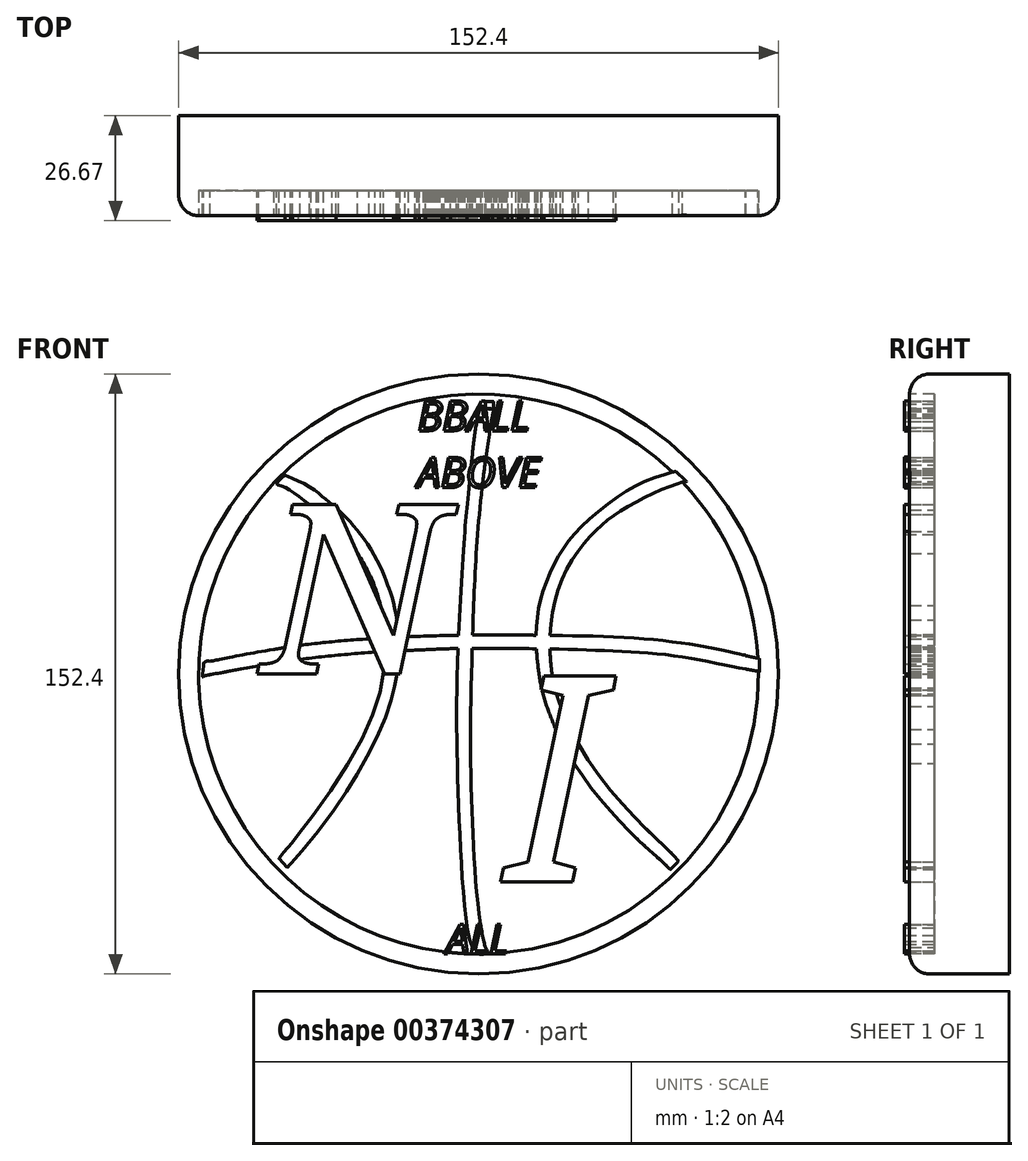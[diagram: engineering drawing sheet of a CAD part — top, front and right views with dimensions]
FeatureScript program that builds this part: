
annotation { "Feature Type Name" : "Feature", "Feature Type Description" : "" }
export const myFeature = defineFeature(function(context is Context, id is Id, definition is map)
    precondition{}
    {
        {
            var Q0;
            Q0=qCreatedBy(makeId("Front.planeOp"),FACE);
            var sketch = newSketch(context, id + "F0", { "sketchPlane" : qUnion([Q0])});
            skCircle(sketch, "E0", {"center": v(0, 0) * mm, "radius": 76.2 * mm});
            skSolve(sketch);
        }
        {
            var Q0;
            Q0 = qSketchRegion(id + "F0", true);
            extrude(context, id + "F1", {"entities" : qUnion([Q0]), "depth" : 25.4 * mm});
        }
        {
            var Q0;
            Q0=makeQuery(id+"F1.opExtrude","CAP_EDGE",EDGE,{"disambiguationData":[OSD([sQuery(id+"F0.wireOp",EDGE,"E0")])],"isStart":false});
            fillet(context, id + "F2", {"entities" : qUnion([Q0]), "radius" : 5.08 * mm, "tangentPropagation" : true, "allowEdgeOverflow" : false});
        }
        {
            var Q0;
            Q0=makeQuery(id+"F1.opExtrude","CAP_FACE",FACE,{"disambiguationData":[OSD([sQuery(id+"F0.wireOp",EDGE,"E0")])],"isStart":false});
            extrude(context, id + "F3", {"entities" : qUnion([Q0]), "operationType" : NewBodyOperationType.REMOVE, "oppositeDirection" : true, "depth" : 6.35 * mm});
        }
        {
            var Q0;
            Q0=qCreatedBy(makeId("Front.planeOp"),FACE);
            var sketch = newSketch(context, id + "F4", { "sketchPlane" : qUnion([Q0])});
            skFitSpline(sketch, "E1", {"points": [v(0.43, 67.37) * mm, v(-2.38, 48.32) * mm, v(-3.55, 35.89) * mm, v(-5.39, 2.5) * mm, v(-5.39, -23.76) * mm, v(-3.75, -57.29) * mm, v(0, -71.12) * mm, v(2.35, -70.65) * mm, v(2.07, -70.11) * mm, v(0, -60.03) * mm, v(-1.58, -38.52) * mm, v(-2.06, -14.54) * mm, v(-1.46, 12.15) * mm, v(0.45, 43.52) * mm, v(3.56, 65.82) * mm, v(3.73, 67.22) * mm, v(3.43, 67.3) * mm, v(2.66, 67.36) * mm, v(1.7, 67.42) * mm, v(0.96, 67.42) * mm, v(0.43, 67.37) * mm]});
            skFitSpline(sketch, "E2", {"points": [v(0.43, 67.37) * mm, v(0.96, 69.23) * mm, v(1.24, 69.3) * mm, v(3.73, 69.24) * mm, v(3.73, 69.12) * mm, v(3.73, 67.22) * mm, v(3.43, 67.3) * mm, v(0.96, 67.42) * mm, v(0.43, 67.37) * mm]});
            skFitSpline(sketch, "E3", {"points": [v(-51.3, 48.31) * mm, v(-49.2, 50.52) * mm, v(-49.04, 50.46) * mm, v(-43.77, 48.04) * mm, v(-39.04, 44.55) * mm, v(-36.11, 42.16) * mm, v(-32.27, 38.2) * mm, v(-28.61, 33.53) * mm, v(-24.96, 27.16) * mm, v(-23.18, 22.83) * mm, v(-22.06, 19.63) * mm, v(-20.74, 13.35) * mm, v(-20.42, 9.42) * mm, v(-20.3, 5.87) * mm, v(-20.63, 0.66) * mm, v(-21.52, -3.9) * mm, v(-23.9, -11.73) * mm, v(-29.79, -23.62) * mm, v(-36.43, -34.1) * mm, v(-46.85, -47.27) * mm, v(-48.45, -49.12) * mm, v(-48.49, -49.2) * mm, v(-50.8, -46.83) * mm, v(-50.84, -46.8) * mm, v(-48.26, -43.86) * mm, v(-46.16, -41.3) * mm, v(-34.02, -24.2) * mm, v(-25.35, -5.66) * mm, v(-23.77, 5.77) * mm, v(-24.56, 15.63) * mm, v(-28.4, 26.67) * mm, v(-36.59, 37.72) * mm, v(-44.97, 44.62) * mm, v(-50.1, 47.77) * mm, v(-51.3, 48.31) * mm]});
            skFitSpline(sketch, "E4", {"points": [v(49.97, 51.4) * mm, v(43.74, 49.51) * mm, v(35.15, 44.88) * mm, v(25.97, 37.27) * mm, v(21.1, 31.24) * mm, v(17.5, 24.26) * mm, v(15.31, 16.84) * mm, v(14.6, 9.88) * mm, v(15.03, 2.38) * mm, v(16.3, -4.84) * mm, v(18.7, -11.92) * mm, v(21.92, -18.8) * mm, v(28.03, -28.15) * mm, v(35.89, -37.45) * mm, v(43, -44.46) * mm, v(48.51, -49.6) * mm, v(48.64, -49.74) * mm, v(50.75, -47.69) * mm, v(50.82, -47.62) * mm, v(48.93, -45.5) * mm, v(41.94, -38.73) * mm, v(30.38, -25.58) * mm, v(21.37, -9.65) * mm, v(18.22, 4.2) * mm, v(20.6, 22.67) * mm, v(28.83, 35.42) * mm, v(35.86, 41.28) * mm, v(46.79, 46.95) * mm, v(52.6, 48.86) * mm, v(52.81, 48.9) * mm, v(50.42, 51.15) * mm, v(49.97, 51.4) * mm]});
            skFitSpline(sketch, "E5", {"points": [v(-68.51, 3.2) * mm, v(-68.41, 0) * mm, v(-68.4, 0) * mm, v(-56.64, 2.03) * mm, v(-36.74, 4.8) * mm, v(-23.77, 5.77) * mm, v(-20.3, 5.87) * mm, v(-5.24, 6.48) * mm, v(14.69, 6.44) * mm, v(33.73, 5.87) * mm, v(51.34, 4.39) * mm, v(66.6, 1.45) * mm, v(71.32, 0.61) * mm, v(71.34, 0.61) * mm, v(71.35, 3.86) * mm, v(71.26, 3.94) * mm, v(64.45, 5.36) * mm, v(53.3, 7.57) * mm, v(40.26, 8.93) * mm, v(28.65, 9.56) * mm, v(18.16, 9.8) * mm, v(5.3, 9.9) * mm, v(-1.53, 9.86) * mm, v(-7.08, 9.78) * mm, v(-18.44, 9.42) * mm, v(-20.42, 9.42) * mm, v(-27.54, 8.86) * mm, v(-35.46, 8.26) * mm, v(-48.96, 6.71) * mm, v(-64.6, 3.96) * mm, v(-68.02, 3.27) * mm, v(-68.48, 3.2) * mm, v(-68.51, 3.2) * mm, v(-68.51, 3.2) * mm]});
            skSolve(sketch);
        }
        {
            var Q0;
            {var subQ0=sQuery(id+"F4.wireOp",EDGE,"E5");var subQ1=sQuery(id+"F4.wireOp",EDGE,"E1");var subQ2=makeQuery(id+"F4.imprint","INTERSECT",VERTEX,{"disambiguationData":[OD(1.0)],"derivedFrom":[subQ1,subQ0]});Q0=makeQuery(id+"F4.imprint","IMPRINT",FACE,{"disambiguationData":[TD([[makeQuery(id+"F4.imprint","IMPRINT",EDGE,{"disambiguationData":[TD([[subQ2,-1.0]])],"derivedFrom":subQ1}),1.0]])]});}
            var Q1;
            {var subQ0=sQuery(id+"F4.wireOp",EDGE,"E5");var subQ1=sQuery(id+"F4.wireOp",EDGE,"E3");var subQ2=makeQuery(id+"F4.imprint","INTERSECT",VERTEX,{"disambiguationData":[OD(0.0)],"derivedFrom":[subQ1,subQ0]});Q1=makeQuery(id+"F4.imprint","IMPRINT",FACE,{"disambiguationData":[TD([[makeQuery(id+"F4.imprint","IMPRINT",EDGE,{"disambiguationData":[TD([[subQ2,-1.0]])],"derivedFrom":subQ1}),-1.0]])]});}
            var Q2;
            {var subQ0=sQuery(id+"F4.wireOp",EDGE,"E5");var subQ1=sQuery(id+"F4.wireOp",EDGE,"E3");var subQ2=makeQuery(id+"F4.imprint","INTERSECT",VERTEX,{"disambiguationData":[OD(2.0)],"derivedFrom":[subQ1,subQ0]});Q2=makeQuery(id+"F4.imprint","IMPRINT",FACE,{"disambiguationData":[TD([[makeQuery(id+"F4.imprint","IMPRINT",EDGE,{"disambiguationData":[TD([[subQ2,-1.0]])],"derivedFrom":subQ1}),1.0]])]});}
            var Q3;
            {var subQ0=sQuery(id+"F4.wireOp",EDGE,"E5");var subQ1=sQuery(id+"F4.wireOp",EDGE,"E3");var subQ2=makeQuery(id+"F4.imprint","INTERSECT",VERTEX,{"disambiguationData":[OD(1.0)],"derivedFrom":[subQ1,subQ0]});Q3=makeQuery(id+"F4.imprint","IMPRINT",FACE,{"disambiguationData":[TD([[makeQuery(id+"F4.imprint","IMPRINT",EDGE,{"disambiguationData":[TD([[subQ2,1.0]])],"derivedFrom":subQ1}),-1.0]])]});}
            var Q4;
            {var subQ0=sQuery(id+"F4.wireOp",EDGE,"E5");var subQ1=sQuery(id+"F4.wireOp",EDGE,"E4");var subQ2=makeQuery(id+"F4.imprint","INTERSECT",VERTEX,{"disambiguationData":[OD(0.0)],"derivedFrom":[subQ1,subQ0]});Q4=makeQuery(id+"F4.imprint","IMPRINT",FACE,{"disambiguationData":[TD([[makeQuery(id+"F4.imprint","IMPRINT",EDGE,{"disambiguationData":[TD([[subQ2,-1.0]])],"derivedFrom":subQ1}),1.0]])]});}
            var Q5;
            {var subQ0=sQuery(id+"F4.wireOp",EDGE,"E5");var subQ1=sQuery(id+"F4.wireOp",EDGE,"E4");var subQ2=makeQuery(id+"F4.imprint","INTERSECT",VERTEX,{"disambiguationData":[OD(2.0)],"derivedFrom":[subQ1,subQ0]});Q5=makeQuery(id+"F4.imprint","IMPRINT",FACE,{"disambiguationData":[TD([[makeQuery(id+"F4.imprint","IMPRINT",EDGE,{"disambiguationData":[TD([[subQ2,-1.0]])],"derivedFrom":subQ1}),-1.0]])]});}
            var Q6;
            {var subQ0=sQuery(id+"F4.wireOp",EDGE,"E5");var subQ1=sQuery(id+"F4.wireOp",EDGE,"E4");var subQ2=makeQuery(id+"F4.imprint","INTERSECT",VERTEX,{"disambiguationData":[OD(1.0)],"derivedFrom":[subQ1,subQ0]});Q6=makeQuery(id+"F4.imprint","IMPRINT",FACE,{"disambiguationData":[TD([[makeQuery(id+"F4.imprint","IMPRINT",EDGE,{"disambiguationData":[TD([[subQ2,1.0]])],"derivedFrom":subQ1}),1.0]])]});}
            var Q7;
            {var subQ0=sQuery(id+"F4.wireOp",EDGE,"E5");var subQ1=sQuery(id+"F4.wireOp",EDGE,"E1");var subQ2=makeQuery(id+"F4.imprint","INTERSECT",VERTEX,{"disambiguationData":[OD(0.0)],"derivedFrom":[subQ1,subQ0]});Q7=makeQuery(id+"F4.imprint","IMPRINT",FACE,{"disambiguationData":[TD([[makeQuery(id+"F4.imprint","IMPRINT",EDGE,{"disambiguationData":[TD([[subQ2,-1.0]])],"derivedFrom":subQ1}),-1.0]])]});}
            var Q8;
            {var subQ0=sQuery(id+"F4.wireOp",EDGE,"E5");var subQ1=sQuery(id+"F4.wireOp",EDGE,"E1");var subQ2=makeQuery(id+"F4.imprint","INTERSECT",VERTEX,{"disambiguationData":[OD(2.0)],"derivedFrom":[subQ1,subQ0]});Q8=makeQuery(id+"F4.imprint","IMPRINT",FACE,{"disambiguationData":[TD([[makeQuery(id+"F4.imprint","IMPRINT",EDGE,{"disambiguationData":[TD([[subQ2,-1.0]])],"derivedFrom":subQ1}),-1.0]])]});}
            var Q9;
            {var subQ0=sQuery(id+"F4.wireOp",EDGE,"E2");var subQ1=sQuery(id+"F4.wireOp",EDGE,"E1");var subQ2=makeQuery(id+"F4.imprint","INTERSECT",VERTEX,{"disambiguationData":[OD(1.0)],"derivedFrom":[subQ1,subQ0]});Q9=makeQuery(id+"F4.imprint","IMPRINT",FACE,{"disambiguationData":[TD([[makeQuery(id+"F4.imprint","IMPRINT",EDGE,{"disambiguationData":[TD([[subQ2,-1.0]])],"derivedFrom":subQ1}),1.0]])]});}
            var Q10;
            {var subQ0=sQuery(id+"F4.wireOp",EDGE,"E2");var subQ1=sQuery(id+"F4.wireOp",EDGE,"E1");var subQ2=makeQuery(id+"F4.imprint","INTERSECT",VERTEX,{"disambiguationData":[OD(0.0)],"derivedFrom":[subQ1,subQ0]});Q10=makeQuery(id+"F4.imprint","IMPRINT",FACE,{"disambiguationData":[TD([[makeQuery(id+"F4.imprint","IMPRINT",EDGE,{"disambiguationData":[TD([[subQ2,1.0]])],"derivedFrom":subQ1}),1.0]])]});}
            var Q11;
            {var subQ0=sQuery(id+"F4.wireOp",EDGE,"E2");var subQ1=sQuery(id+"F4.wireOp",EDGE,"E1");var subQ2=makeQuery(id+"F4.imprint","INTERSECT",VERTEX,{"disambiguationData":[OD(1.0)],"derivedFrom":[subQ1,subQ0]});Q11=makeQuery(id+"F4.imprint","IMPRINT",FACE,{"disambiguationData":[TD([[makeQuery(id+"F4.imprint","IMPRINT",EDGE,{"disambiguationData":[TD([[subQ2,-1.0]])],"derivedFrom":subQ1}),-1.0]])]});}
            var Q12;
            {var subQ1=sQuery(id+"F4.wireOp",EDGE,"E1");var subQ4=sQuery(id+"F4.wireOp",EDGE,"E5");var subQ5=makeQuery(id+"F4.imprint","INTERSECT",VERTEX,{"disambiguationData":[OD(0.0)],"derivedFrom":[subQ1,subQ4]});Q12=makeQuery(id+"F4.imprint","IMPRINT",FACE,{"disambiguationData":[TD([[makeQuery(id+"F4.imprint","IMPRINT",EDGE,{"disambiguationData":[TD([[subQ5,1.0]])],"derivedFrom":subQ1}),1.0]])]});}
            var Q13;
            {var subQ0=sQuery(id+"F4.wireOp",EDGE,"E5");var subQ1=sQuery(id+"F4.wireOp",EDGE,"E1");var subQ2=makeQuery(id+"F4.imprint","INTERSECT",VERTEX,{"disambiguationData":[OD(0.0)],"derivedFrom":[subQ1,subQ0]});Q13=makeQuery(id+"F4.imprint","IMPRINT",FACE,{"disambiguationData":[TD([[makeQuery(id+"F4.imprint","IMPRINT",EDGE,{"disambiguationData":[TD([[subQ2,-1.0]])],"derivedFrom":subQ1}),1.0]])]});}
            var Q14;
            {var subQ0=sQuery(id+"F4.wireOp",EDGE,"E5");var subQ1=sQuery(id+"F4.wireOp",EDGE,"E3");var subQ2=makeQuery(id+"F4.imprint","INTERSECT",VERTEX,{"disambiguationData":[OD(0.0)],"derivedFrom":[subQ1,subQ0]});Q14=makeQuery(id+"F4.imprint","IMPRINT",FACE,{"disambiguationData":[TD([[makeQuery(id+"F4.imprint","IMPRINT",EDGE,{"disambiguationData":[TD([[subQ2,1.0]])],"derivedFrom":subQ1}),-1.0]])]});}
            var Q15;
            {var subQ0=sQuery(id+"F4.wireOp",EDGE,"E5");var subQ1=sQuery(id+"F4.wireOp",EDGE,"E4");var subQ2=makeQuery(id+"F4.imprint","INTERSECT",VERTEX,{"disambiguationData":[OD(0.0)],"derivedFrom":[subQ1,subQ0]});Q15=makeQuery(id+"F4.imprint","IMPRINT",FACE,{"disambiguationData":[TD([[makeQuery(id+"F4.imprint","IMPRINT",EDGE,{"disambiguationData":[TD([[subQ2,1.0]])],"derivedFrom":subQ1}),1.0]])]});}
            extrude(context, id + "F5", {"entities" : qUnion([Q0, Q1, Q2, Q3, Q4, Q5, Q6, Q7, Q8, Q9, Q10, Q11, Q12, Q13, Q14, Q15]), "operationType" : NewBodyOperationType.ADD, "depth" : 25.4 * mm});
        }
        {
            var Q0;
            Q0=qCreatedBy(makeId("Front.planeOp"),FACE);
            var sketch = newSketch(context, id + "F6", { "sketchPlane" : qUnion([Q0])});
            skFitSpline(sketch, "E6", {"points": [v(-69.92, 2.6) * mm, v(-70.1, -0.84) * mm, v(-69.9, -0.68) * mm, v(-67.28, 0) * mm, v(-59.4, 1.42) * mm, v(-45.16, 3.72) * mm, v(-23.73, 5.73) * mm, v(-4.99, 6.47) * mm, v(4.26, 6.5) * mm, v(31.3, 6.07) * mm, v(54, 4.1) * mm, v(67.83, 1.25) * mm, v(67.93, 1.25) * mm, v(67.82, 4.75) * mm, v(67.61, 4.84) * mm, v(59.91, 6.46) * mm, v(38.53, 9.19) * mm, v(12.88, 9.82) * mm, v(-1.6, 9.88) * mm, v(-28.75, 8.88) * mm, v(-55.01, 5.69) * mm, v(-68.06, 3.22) * mm, v(-68.88, 3.3) * mm, v(-69.95, 2.75) * mm, v(-69.92, 2.6) * mm]});
            skSolve(sketch);
        }
        {
            var Q0;
            Q0 = qSketchRegion(id + "F6", true);
            extrude(context, id + "F7", {"entities" : qUnion([Q0]), "depth" : 25.4 * mm});
        }
        {
            var Q0;
            Q0 = qSketchRegion(id + "F4", true);
            extrude(context, id + "F8", {"entities" : qUnion([Q0]), "depth" : 25.4 * mm});
        }
        {
            var Q0;
            Q0 = qSketchRegion(id + "F4", true);
            extrude(context, id + "F9", {"entities" : qUnion([Q0]), "depth" : 25.4 * mm});
        }
        {
            var Q0;
            {var subQ0=sQuery(id+"F4.wireOp",EDGE,"E5");var subQ1=sQuery(id+"F4.wireOp",EDGE,"E1");var subQ2=makeQuery(id+"F4.imprint","INTERSECT",VERTEX,{"disambiguationData":[OD(1.0)],"derivedFrom":[subQ1,subQ0]});var subQ3=sQuery(id+"F4.wireOp",EDGE,"E3");var subQ4=makeQuery(id+"F4.imprint","INTERSECT",VERTEX,{"disambiguationData":[OD(0.0)],"derivedFrom":[subQ3,subQ0]});var subQ5=makeQuery(id+"F4.imprint","INTERSECT",VERTEX,{"disambiguationData":[OD(1.0)],"derivedFrom":[subQ3,subQ0]});var subQ7=makeQuery(id+"F4.imprint","INTERSECT",VERTEX,{"disambiguationData":[OD(2.0)],"derivedFrom":[subQ3,subQ0]});var subQ8=sQuery(id+"F4.wireOp",EDGE,"E2");var subQ9=makeQuery(id+"F4.imprint","INTERSECT",VERTEX,{"disambiguationData":[OD(0.0)],"derivedFrom":[subQ1,subQ8]});var subQ11=sQuery(id+"F0.wireOp",EDGE,"E0");var subQ12=sQuery(id+"F4.wireOp",EDGE,"E4");var subQ13=makeQuery(id+"F4.imprint","INTERSECT",VERTEX,{"disambiguationData":[OD(1.0)],"derivedFrom":[subQ12,subQ0]});var subQ14=makeQuery(id+"F4.imprint","INTERSECT",VERTEX,{"disambiguationData":[OD(0.0)],"derivedFrom":[subQ1,subQ0]});var subQ15=makeQuery(id+"F4.imprint","INTERSECT",VERTEX,{"disambiguationData":[OD(3.0)],"derivedFrom":[subQ1,subQ0]});Q0=makeQuery(id+"F5.boolean.opBoolean","SPLIT",FACE,{"disambiguationData":[TD([makeQuery(id+"F3.boolean.opBoolean","COPY",FACE,{"derivedFrom":makeQuery(id+"F3.opExtrude","SWEPT_FACE",FACE,{"disambiguationData":[OSD([subQ11])]})}),makeQuery(id+"F5.opExtrude","SWEPT_FACE",FACE,{"disambiguationData":[OSD([subQ1]),TDD([makeQuery(id+"F4.imprint","IMPRINT",EDGE,{"disambiguationData":[TD([[subQ14,1.0]])],"derivedFrom":subQ1})])]}),makeQuery(id+"F5.opExtrude","SWEPT_FACE",FACE,{"disambiguationData":[OSD([subQ1]),TDD([makeQuery(id+"F4.imprint","IMPRINT",EDGE,{"disambiguationData":[TD([[subQ2,-1.0]])],"derivedFrom":subQ1})])]}),makeQuery(id+"F5.opExtrude","SWEPT_FACE",FACE,{"disambiguationData":[OSD([subQ1]),TDD([makeQuery(id+"F4.imprint","IMPRINT",EDGE,{"disambiguationData":[TD([[subQ15,-1.0]])],"derivedFrom":subQ1})])]}),makeQuery(id+"F5.opExtrude","SWEPT_FACE",FACE,{"disambiguationData":[OSD([subQ8]),TDD([makeQuery(id+"F4.imprint","IMPRINT",EDGE,{"disambiguationData":[TD([[subQ9,-1.0]])],"derivedFrom":subQ8})])]}),makeQuery(id+"F5.opExtrude","SWEPT_FACE",FACE,{"disambiguationData":[OSD([subQ3]),TDD([makeQuery(id+"F4.imprint","IMPRINT",EDGE,{"disambiguationData":[TD([[subQ4,-1.0]])],"derivedFrom":subQ3})])]}),makeQuery(id+"F5.opExtrude","SWEPT_FACE",FACE,{"disambiguationData":[OSD([subQ3]),TDD([makeQuery(id+"F4.imprint","IMPRINT",EDGE,{"disambiguationData":[TD([[subQ5,1.0]])],"derivedFrom":subQ3})])]}),makeQuery(id+"F5.opExtrude","SWEPT_FACE",FACE,{"disambiguationData":[OSD([subQ12]),TDD([makeQuery(id+"F4.imprint","IMPRINT",EDGE,{"disambiguationData":[TD([[subQ13,1.0]])],"derivedFrom":subQ12})])]}),makeQuery(id+"F5.opExtrude","SWEPT_FACE",FACE,{"disambiguationData":[OSD([subQ0]),TDD([makeQuery(id+"F4.imprint","IMPRINT",EDGE,{"disambiguationData":[TD([[subQ2,1.0]])],"derivedFrom":subQ0})])]}),makeQuery(id+"F5.opExtrude","SWEPT_FACE",FACE,{"disambiguationData":[OSD([subQ0]),TDD([makeQuery(id+"F4.imprint","IMPRINT",EDGE,{"disambiguationData":[TD([[subQ15,1.0]])],"derivedFrom":subQ0})])]}),makeQuery(id+"F5.opExtrude","SWEPT_FACE",FACE,{"disambiguationData":[OSD([subQ0]),TDD([makeQuery(id+"F4.imprint","IMPRINT",EDGE,{"disambiguationData":[TD([[subQ14,-1.0]])],"derivedFrom":subQ0})])]}),makeQuery(id+"F5.opExtrude","SWEPT_FACE",FACE,{"disambiguationData":[OSD([subQ0]),TDD([makeQuery(id+"F4.imprint","IMPRINT",EDGE,{"disambiguationData":[TD([[subQ7,1.0]])],"derivedFrom":subQ0})])]})])],"derivedFrom":makeQuery(id+"F3.boolean.opBoolean","COPY",FACE,{"derivedFrom":makeQuery(id+"F3.opExtrude","CAP_FACE",FACE,{"disambiguationData":[OSD([subQ11])],"isStart":false})})});}
            var sketch = newSketch(context, id + "F10", { "sketchPlane" : qUnion([Q0])});
            skText(sketch, "E7", { "text": "N", "fontName": "NotoSerif-Italic.ttf"});
            const initialGuessF10  = {"E7": [-0.05508, 0, 1, 0, 0.04348]};
            skSetInitialGuess(sketch, initialGuessF10);
            skSolve(sketch);
        }
        {
            var Q0;
            Q0 = qSketchRegion(id + "F10", true);
            extrude(context, id + "F11", {"entities" : qUnion([Q0]), "operationType" : NewBodyOperationType.ADD, "depth" : 7.62 * mm});
        }
        {
            var Q0;
            {var subQ0=sQuery(id+"F4.wireOp",EDGE,"E5");var subQ1=sQuery(id+"F4.wireOp",EDGE,"E4");var subQ2=makeQuery(id+"F4.imprint","INTERSECT",VERTEX,{"disambiguationData":[OD(0.0)],"derivedFrom":[subQ1,subQ0]});var subQ3=makeQuery(id+"F4.imprint","INTERSECT",VERTEX,{"disambiguationData":[OD(2.0)],"derivedFrom":[subQ1,subQ0]});var subQ4=sQuery(id+"F0.wireOp",EDGE,"E0");var subQ5=sQuery(id+"F4.wireOp",EDGE,"E1");var subQ6=makeQuery(id+"F4.imprint","INTERSECT",VERTEX,{"disambiguationData":[OD(2.0)],"derivedFrom":[subQ5,subQ0]});Q0=makeQuery(id+"F5.boolean.opBoolean","SPLIT",FACE,{"disambiguationData":[TD([makeQuery(id+"F3.boolean.opBoolean","COPY",FACE,{"derivedFrom":makeQuery(id+"F3.opExtrude","SWEPT_FACE",FACE,{"disambiguationData":[OSD([subQ4])]})}),makeQuery(id+"F5.opExtrude","SWEPT_FACE",FACE,{"disambiguationData":[OSD([subQ5]),TDD([makeQuery(id+"F4.imprint","IMPRINT",EDGE,{"disambiguationData":[TD([[makeQuery(id+"F4.imprint","INTERSECT",VERTEX,{"disambiguationData":[OD(1.0)],"derivedFrom":[subQ5,subQ0]}),-1.0]])],"derivedFrom":subQ5})])]}),makeQuery(id+"F5.opExtrude","SWEPT_FACE",FACE,{"disambiguationData":[OSD([subQ1]),TDD([makeQuery(id+"F4.imprint","IMPRINT",EDGE,{"disambiguationData":[TD([[subQ2,-1.0]])],"derivedFrom":subQ1})])]}),makeQuery(id+"F5.opExtrude","SWEPT_FACE",FACE,{"disambiguationData":[OSD([subQ0]),TDD([makeQuery(id+"F4.imprint","IMPRINT",EDGE,{"disambiguationData":[TD([[subQ6,-1.0]])],"derivedFrom":subQ0})])]}),makeQuery(id+"F5.opExtrude","SWEPT_FACE",FACE,{"disambiguationData":[OSD([subQ0]),TDD([makeQuery(id+"F4.imprint","IMPRINT",EDGE,{"disambiguationData":[TD([[subQ3,-1.0]])],"derivedFrom":subQ0})])]})])],"derivedFrom":makeQuery(id+"F3.boolean.opBoolean","COPY",FACE,{"derivedFrom":makeQuery(id+"F3.opExtrude","CAP_FACE",FACE,{"disambiguationData":[OSD([subQ4])],"isStart":false})})});}
            var sketch = newSketch(context, id + "F12", { "sketchPlane" : qUnion([Q0])});
            skText(sketch, "E8", { "text": "I", "fontName": "NotoSans-Italic.ttf"});
            const initialGuessF12  = {"E8": [0.007, -0.05279, 1, 0, 0.05279]};
            skSetInitialGuess(sketch, initialGuessF12);
            skSolve(sketch);
        }
        {
            var Q0;
            Q0 = qSketchRegion(id + "F12", true);
            extrude(context, id + "F13", {"entities" : qUnion([Q0]), "operationType" : NewBodyOperationType.ADD, "depth" : 7.62 * mm});
        }
        {
            var Q0;
            {var subQ0=sQuery(id+"F4.wireOp",EDGE,"E5");var subQ1=sQuery(id+"F4.wireOp",EDGE,"E1");var subQ2=makeQuery(id+"F4.imprint","INTERSECT",VERTEX,{"disambiguationData":[OD(0.0)],"derivedFrom":[subQ1,subQ0]});var subQ3=sQuery(id+"F4.wireOp",EDGE,"E2");var subQ4=makeQuery(id+"F4.imprint","INTERSECT",VERTEX,{"disambiguationData":[OD(0.0)],"derivedFrom":[subQ1,subQ3]});var subQ5=makeQuery(id+"F5.opExtrude","SWEPT_FACE",FACE,{"disambiguationData":[OSD([subQ1]),TDD([makeQuery(id+"F4.imprint","IMPRINT",EDGE,{"disambiguationData":[TD([[subQ2,1.0]])],"derivedFrom":subQ1})])]});var subQ7=makeQuery(id+"F5.opExtrude","SWEPT_FACE",FACE,{"disambiguationData":[OSD([subQ3]),TDD([makeQuery(id+"F4.imprint","IMPRINT",EDGE,{"disambiguationData":[TD([[subQ4,-1.0]])],"derivedFrom":subQ3})])]});var subQ8=sQuery(id+"F4.wireOp",EDGE,"E3");var subQ9=makeQuery(id+"F4.imprint","INTERSECT",VERTEX,{"disambiguationData":[OD(2.0)],"derivedFrom":[subQ8,subQ0]});var subQ11=makeQuery(id+"F5.opExtrude","SWEPT_FACE",FACE,{"disambiguationData":[OSD([subQ0]),TDD([makeQuery(id+"F4.imprint","IMPRINT",EDGE,{"disambiguationData":[TD([[subQ9,1.0]])],"derivedFrom":subQ0})])]});var subQ12=makeQuery(id+"F4.imprint","INTERSECT",VERTEX,{"disambiguationData":[OD(3.0)],"derivedFrom":[subQ1,subQ0]});var subQ13=makeQuery(id+"F5.opExtrude","SWEPT_FACE",FACE,{"disambiguationData":[OSD([subQ1]),TDD([makeQuery(id+"F4.imprint","IMPRINT",EDGE,{"disambiguationData":[TD([[subQ12,-1.0]])],"derivedFrom":subQ1})])]});var subQ14=sQuery(id+"F4.wireOp",EDGE,"E4");var subQ15=makeQuery(id+"F4.imprint","INTERSECT",VERTEX,{"disambiguationData":[OD(1.0)],"derivedFrom":[subQ14,subQ0]});var subQ16=makeQuery(id+"F5.opExtrude","SWEPT_FACE",FACE,{"disambiguationData":[OSD([subQ0]),TDD([makeQuery(id+"F4.imprint","IMPRINT",EDGE,{"disambiguationData":[TD([[subQ12,1.0]])],"derivedFrom":subQ0})])]});var subQ17=makeQuery(id+"F4.imprint","INTERSECT",VERTEX,{"disambiguationData":[OD(1.0)],"derivedFrom":[subQ1,subQ0]});var subQ18=makeQuery(id+"F5.opExtrude","SWEPT_FACE",FACE,{"disambiguationData":[OSD([subQ1]),TDD([makeQuery(id+"F4.imprint","IMPRINT",EDGE,{"disambiguationData":[TD([[subQ17,-1.0]])],"derivedFrom":subQ1})])]});var subQ19=makeQuery(id+"F5.opExtrude","SWEPT_FACE",FACE,{"disambiguationData":[OSD([subQ14]),TDD([makeQuery(id+"F4.imprint","IMPRINT",EDGE,{"disambiguationData":[TD([[subQ15,1.0]])],"derivedFrom":subQ14})])]});var subQ20=sQuery(id+"F0.wireOp",EDGE,"E0");var subQ21=makeQuery(id+"F3.boolean.opBoolean","COPY",FACE,{"derivedFrom":makeQuery(id+"F3.opExtrude","SWEPT_FACE",FACE,{"disambiguationData":[OSD([subQ20])]})});var subQ22=makeQuery(id+"F4.imprint","INTERSECT",VERTEX,{"disambiguationData":[OD(0.0)],"derivedFrom":[subQ8,subQ0]});var subQ23=makeQuery(id+"F5.opExtrude","SWEPT_FACE",FACE,{"disambiguationData":[OSD([subQ8]),TDD([makeQuery(id+"F4.imprint","IMPRINT",EDGE,{"disambiguationData":[TD([[subQ22,-1.0]])],"derivedFrom":subQ8})])]});var subQ24=makeQuery(id+"F4.imprint","INTERSECT",VERTEX,{"disambiguationData":[OD(1.0)],"derivedFrom":[subQ8,subQ0]});var subQ25=makeQuery(id+"F5.opExtrude","SWEPT_FACE",FACE,{"disambiguationData":[OSD([subQ8]),TDD([makeQuery(id+"F4.imprint","IMPRINT",EDGE,{"disambiguationData":[TD([[subQ24,1.0]])],"derivedFrom":subQ8})])]});var subQ26=makeQuery(id+"F5.opExtrude","SWEPT_FACE",FACE,{"disambiguationData":[OSD([subQ0]),TDD([makeQuery(id+"F4.imprint","IMPRINT",EDGE,{"disambiguationData":[TD([[subQ17,1.0]])],"derivedFrom":subQ0})])]});Q0=makeQuery(id+"F11.boolean.opBoolean","SPLIT",FACE,{"disambiguationData":[TD([subQ21,subQ5,subQ18,subQ13,subQ7,subQ23,subQ25,subQ19,subQ26,subQ16,subQ11,makeQuery(id+"F7.opExtrude","SWEPT_FACE",FACE,{"disambiguationData":[OSD([sQuery(id+"F6.wireOp",EDGE,"E6")])]}),makeQuery(id+"F11.opExtrude","SWEPT_FACE",FACE,{"disambiguationData":[OSD([sQuery(id+"F10.wireOp",EDGE,"E7.sketch_text.stroke-0")])]}),makeQuery(id+"F11.opExtrude","SWEPT_FACE",FACE,{"disambiguationData":[OSD([sQuery(id+"F10.wireOp",EDGE,"E7.sketch_text.stroke-1")])]}),makeQuery(id+"F11.opExtrude","SWEPT_FACE",FACE,{"disambiguationData":[OSD([sQuery(id+"F10.wireOp",EDGE,"E7.sketch_text.stroke-2")])]}),makeQuery(id+"F11.opExtrude","SWEPT_FACE",FACE,{"disambiguationData":[OSD([sQuery(id+"F10.wireOp",EDGE,"E7.sketch_text.stroke-3")])]}),makeQuery(id+"F11.opExtrude","SWEPT_FACE",FACE,{"disambiguationData":[OSD([sQuery(id+"F10.wireOp",EDGE,"E7.sketch_text.stroke-4")])]}),makeQuery(id+"F11.opExtrude","SWEPT_FACE",FACE,{"disambiguationData":[OSD([sQuery(id+"F10.wireOp",EDGE,"E7.sketch_text.stroke-5")])]}),makeQuery(id+"F11.opExtrude","SWEPT_FACE",FACE,{"disambiguationData":[OSD([sQuery(id+"F10.wireOp",EDGE,"E7.sketch_text.stroke-6")])]}),makeQuery(id+"F11.opExtrude","SWEPT_FACE",FACE,{"disambiguationData":[OSD([sQuery(id+"F10.wireOp",EDGE,"E7.sketch_text.stroke-7")])]}),makeQuery(id+"F11.opExtrude","SWEPT_FACE",FACE,{"disambiguationData":[OSD([sQuery(id+"F10.wireOp",EDGE,"E7.sketch_text.stroke-8")])]}),makeQuery(id+"F11.opExtrude","SWEPT_FACE",FACE,{"disambiguationData":[OSD([sQuery(id+"F10.wireOp",EDGE,"E7.sketch_text.stroke-9")])]}),makeQuery(id+"F11.opExtrude","SWEPT_FACE",FACE,{"disambiguationData":[OSD([sQuery(id+"F10.wireOp",EDGE,"E7.sketch_text.stroke-10")])]}),makeQuery(id+"F11.opExtrude","SWEPT_FACE",FACE,{"disambiguationData":[OSD([sQuery(id+"F10.wireOp",EDGE,"E7.sketch_text.stroke-11")])]}),makeQuery(id+"F11.opExtrude","SWEPT_FACE",FACE,{"disambiguationData":[OSD([sQuery(id+"F10.wireOp",EDGE,"E7.sketch_text.stroke-14")])]}),makeQuery(id+"F11.opExtrude","SWEPT_FACE",FACE,{"disambiguationData":[OSD([sQuery(id+"F10.wireOp",EDGE,"E7.sketch_text.stroke-15")])]}),makeQuery(id+"F11.opExtrude","SWEPT_FACE",FACE,{"disambiguationData":[OSD([sQuery(id+"F10.wireOp",EDGE,"E7.sketch_text.stroke-16")])]}),makeQuery(id+"F11.opExtrude","SWEPT_FACE",FACE,{"disambiguationData":[OSD([sQuery(id+"F10.wireOp",EDGE,"E7.sketch_text.stroke-17")])]}),makeQuery(id+"F11.opExtrude","SWEPT_FACE",FACE,{"disambiguationData":[OSD([sQuery(id+"F10.wireOp",EDGE,"E7.sketch_text.stroke-18")])]}),makeQuery(id+"F11.opExtrude","SWEPT_FACE",FACE,{"disambiguationData":[OSD([sQuery(id+"F10.wireOp",EDGE,"E7.sketch_text.stroke-21")])]}),makeQuery(id+"F11.opExtrude","SWEPT_FACE",FACE,{"disambiguationData":[OSD([sQuery(id+"F10.wireOp",EDGE,"E7.sketch_text.stroke-22")])]}),makeQuery(id+"F11.opExtrude","SWEPT_FACE",FACE,{"disambiguationData":[OSD([sQuery(id+"F10.wireOp",EDGE,"E7.sketch_text.stroke-23")])]}),makeQuery(id+"F11.opExtrude","SWEPT_FACE",FACE,{"disambiguationData":[OSD([sQuery(id+"F10.wireOp",EDGE,"E7.sketch_text.stroke-24")])]}),makeQuery(id+"F11.opExtrude","SWEPT_FACE",FACE,{"disambiguationData":[OSD([sQuery(id+"F10.wireOp",EDGE,"E7.sketch_text.stroke-25")])]}),makeQuery(id+"F11.opExtrude","SWEPT_FACE",FACE,{"disambiguationData":[OSD([sQuery(id+"F10.wireOp",EDGE,"E7.sketch_text.stroke-26")])]}),makeQuery(id+"F11.opExtrude","SWEPT_FACE",FACE,{"disambiguationData":[OSD([sQuery(id+"F10.wireOp",EDGE,"E7.sketch_text.stroke-27")])]}),makeQuery(id+"F11.opExtrude","SWEPT_FACE",FACE,{"disambiguationData":[OSD([sQuery(id+"F10.wireOp",EDGE,"E7.sketch_text.stroke-28")])]}),makeQuery(id+"F11.opExtrude","SWEPT_FACE",FACE,{"disambiguationData":[OSD([sQuery(id+"F10.wireOp",EDGE,"E7.sketch_text.stroke-29")])]})])],"derivedFrom":makeQuery(id+"F5.boolean.opBoolean","SPLIT",FACE,{"disambiguationData":[TD([subQ21,subQ5,subQ18,subQ13,subQ7,subQ23,subQ25,subQ19,subQ26,subQ16,makeQuery(id+"F5.opExtrude","SWEPT_FACE",FACE,{"disambiguationData":[OSD([subQ0]),TDD([makeQuery(id+"F4.imprint","IMPRINT",EDGE,{"disambiguationData":[TD([[subQ2,-1.0]])],"derivedFrom":subQ0})])]}),subQ11])],"derivedFrom":makeQuery(id+"F3.boolean.opBoolean","COPY",FACE,{"derivedFrom":makeQuery(id+"F3.opExtrude","CAP_FACE",FACE,{"disambiguationData":[OSD([subQ20])],"isStart":false})})})});}
            var sketch = newSketch(context, id + "F14", { "sketchPlane" : qUnion([Q0])});
            skText(sketch, "E9", { "text": "BBALL\nABOVE ", "fontName": "OpenSans-Italic.ttf"});
            const initialGuessF14  = {"E9": [-0.01552, 0.06179, 1, 0, 0.00762]};
            skSetInitialGuess(sketch, initialGuessF14);
            skSolve(sketch);
        }
        {
            var Q0;
            Q0 = qSketchRegion(id + "F14", true);
            extrude(context, id + "F15", {"entities" : qUnion([Q0]), "operationType" : NewBodyOperationType.ADD, "depth" : 7.62 * mm});
        }
        {
            var Q0;
            {var subQ0=makeQuery(id+"F7.opExtrude","SWEPT_FACE",FACE,{"disambiguationData":[OSD([sQuery(id+"F6.wireOp",EDGE,"E6")])]});var subQ1=makeQuery(id+"F11.opExtrude","SWEPT_FACE",FACE,{"disambiguationData":[OSD([sQuery(id+"F10.wireOp",EDGE,"E7.sketch_text.stroke-8")])]});var subQ2=sQuery(id+"F4.wireOp",EDGE,"E5");var subQ3=sQuery(id+"F4.wireOp",EDGE,"E1");var subQ4=makeQuery(id+"F4.imprint","INTERSECT",VERTEX,{"disambiguationData":[OD(0.0)],"derivedFrom":[subQ3,subQ2]});var subQ5=sQuery(id+"F4.wireOp",EDGE,"E2");var subQ6=makeQuery(id+"F4.imprint","INTERSECT",VERTEX,{"disambiguationData":[OD(0.0)],"derivedFrom":[subQ3,subQ5]});var subQ7=makeQuery(id+"F5.opExtrude","SWEPT_FACE",FACE,{"disambiguationData":[OSD([subQ3]),TDD([makeQuery(id+"F4.imprint","IMPRINT",EDGE,{"disambiguationData":[TD([[subQ4,1.0]])],"derivedFrom":subQ3})])]});var subQ8=makeQuery(id+"F4.imprint","INTERSECT",VERTEX,{"disambiguationData":[OD(1.0)],"derivedFrom":[subQ3,subQ2]});var subQ9=sQuery(id+"F4.wireOp",EDGE,"E3");var subQ10=makeQuery(id+"F4.imprint","INTERSECT",VERTEX,{"disambiguationData":[OD(0.0)],"derivedFrom":[subQ9,subQ2]});var subQ11=makeQuery(id+"F5.opExtrude","SWEPT_FACE",FACE,{"disambiguationData":[OSD([subQ2]),TDD([makeQuery(id+"F4.imprint","IMPRINT",EDGE,{"disambiguationData":[TD([[subQ8,1.0]])],"derivedFrom":subQ2})])]});var subQ12=makeQuery(id+"F11.opExtrude","SWEPT_FACE",FACE,{"disambiguationData":[OSD([sQuery(id+"F10.wireOp",EDGE,"E7.sketch_text.stroke-7")])]});var subQ13=sQuery(id+"F4.wireOp",EDGE,"E4");var subQ14=makeQuery(id+"F4.imprint","INTERSECT",VERTEX,{"disambiguationData":[OD(1.0)],"derivedFrom":[subQ13,subQ2]});var subQ15=makeQuery(id+"F5.opExtrude","SWEPT_FACE",FACE,{"disambiguationData":[OSD([subQ13]),TDD([makeQuery(id+"F4.imprint","IMPRINT",EDGE,{"disambiguationData":[TD([[subQ14,1.0]])],"derivedFrom":subQ13})])]});var subQ16=makeQuery(id+"F11.opExtrude","SWEPT_FACE",FACE,{"disambiguationData":[OSD([sQuery(id+"F10.wireOp",EDGE,"E7.sketch_text.stroke-6")])]});var subQ17=makeQuery(id+"F11.opExtrude","SWEPT_FACE",FACE,{"disambiguationData":[OSD([sQuery(id+"F10.wireOp",EDGE,"E7.sketch_text.stroke-4")])]});var subQ18=makeQuery(id+"F11.opExtrude","SWEPT_FACE",FACE,{"disambiguationData":[OSD([sQuery(id+"F10.wireOp",EDGE,"E7.sketch_text.stroke-2")])]});var subQ20=makeQuery(id+"F5.opExtrude","SWEPT_FACE",FACE,{"disambiguationData":[OSD([subQ5]),TDD([makeQuery(id+"F4.imprint","IMPRINT",EDGE,{"disambiguationData":[TD([[subQ6,-1.0]])],"derivedFrom":subQ5})])]});var subQ21=makeQuery(id+"F11.opExtrude","SWEPT_FACE",FACE,{"disambiguationData":[OSD([sQuery(id+"F10.wireOp",EDGE,"E7.sketch_text.stroke-14")])]});var subQ22=makeQuery(id+"F4.imprint","INTERSECT",VERTEX,{"disambiguationData":[OD(2.0)],"derivedFrom":[subQ9,subQ2]});var subQ23=makeQuery(id+"F5.opExtrude","SWEPT_FACE",FACE,{"disambiguationData":[OSD([subQ9]),TDD([makeQuery(id+"F4.imprint","IMPRINT",EDGE,{"disambiguationData":[TD([[subQ10,-1.0]])],"derivedFrom":subQ9})])]});var subQ24=makeQuery(id+"F11.opExtrude","SWEPT_FACE",FACE,{"disambiguationData":[OSD([sQuery(id+"F10.wireOp",EDGE,"E7.sketch_text.stroke-3")])]});var subQ26=makeQuery(id+"F5.opExtrude","SWEPT_FACE",FACE,{"disambiguationData":[OSD([subQ2]),TDD([makeQuery(id+"F4.imprint","IMPRINT",EDGE,{"disambiguationData":[TD([[subQ22,1.0]])],"derivedFrom":subQ2})])]});var subQ27=makeQuery(id+"F11.opExtrude","SWEPT_FACE",FACE,{"disambiguationData":[OSD([sQuery(id+"F10.wireOp",EDGE,"E7.sketch_text.stroke-25")])]});var subQ28=makeQuery(id+"F4.imprint","INTERSECT",VERTEX,{"disambiguationData":[OD(3.0)],"derivedFrom":[subQ3,subQ2]});var subQ29=makeQuery(id+"F5.opExtrude","SWEPT_FACE",FACE,{"disambiguationData":[OSD([subQ3]),TDD([makeQuery(id+"F4.imprint","IMPRINT",EDGE,{"disambiguationData":[TD([[subQ28,-1.0]])],"derivedFrom":subQ3})])]});var subQ30=makeQuery(id+"F11.opExtrude","SWEPT_FACE",FACE,{"disambiguationData":[OSD([sQuery(id+"F10.wireOp",EDGE,"E7.sketch_text.stroke-1")])]});var subQ31=makeQuery(id+"F5.opExtrude","SWEPT_FACE",FACE,{"disambiguationData":[OSD([subQ2]),TDD([makeQuery(id+"F4.imprint","IMPRINT",EDGE,{"disambiguationData":[TD([[subQ28,1.0]])],"derivedFrom":subQ2})])]});var subQ32=makeQuery(id+"F5.opExtrude","SWEPT_FACE",FACE,{"disambiguationData":[OSD([subQ3]),TDD([makeQuery(id+"F4.imprint","IMPRINT",EDGE,{"disambiguationData":[TD([[subQ8,-1.0]])],"derivedFrom":subQ3})])]});var subQ33=makeQuery(id+"F11.opExtrude","SWEPT_FACE",FACE,{"disambiguationData":[OSD([sQuery(id+"F10.wireOp",EDGE,"E7.sketch_text.stroke-11")])]});var subQ34=makeQuery(id+"F11.opExtrude","SWEPT_FACE",FACE,{"disambiguationData":[OSD([sQuery(id+"F10.wireOp",EDGE,"E7.sketch_text.stroke-9")])]});var subQ35=makeQuery(id+"F11.opExtrude","SWEPT_FACE",FACE,{"disambiguationData":[OSD([sQuery(id+"F10.wireOp",EDGE,"E7.sketch_text.stroke-5")])]});var subQ36=makeQuery(id+"F11.opExtrude","SWEPT_FACE",FACE,{"disambiguationData":[OSD([sQuery(id+"F10.wireOp",EDGE,"E7.sketch_text.stroke-23")])]});var subQ37=sQuery(id+"F0.wireOp",EDGE,"E0");var subQ38=makeQuery(id+"F3.boolean.opBoolean","COPY",FACE,{"derivedFrom":makeQuery(id+"F3.opExtrude","SWEPT_FACE",FACE,{"disambiguationData":[OSD([subQ37])]})});var subQ39=makeQuery(id+"F11.opExtrude","SWEPT_FACE",FACE,{"disambiguationData":[OSD([sQuery(id+"F10.wireOp",EDGE,"E7.sketch_text.stroke-27")])]});var subQ40=makeQuery(id+"F11.opExtrude","SWEPT_FACE",FACE,{"disambiguationData":[OSD([sQuery(id+"F10.wireOp",EDGE,"E7.sketch_text.stroke-16")])]});var subQ41=makeQuery(id+"F4.imprint","INTERSECT",VERTEX,{"disambiguationData":[OD(1.0)],"derivedFrom":[subQ9,subQ2]});var subQ42=makeQuery(id+"F5.opExtrude","SWEPT_FACE",FACE,{"disambiguationData":[OSD([subQ9]),TDD([makeQuery(id+"F4.imprint","IMPRINT",EDGE,{"disambiguationData":[TD([[subQ41,1.0]])],"derivedFrom":subQ9})])]});var subQ43=makeQuery(id+"F11.opExtrude","SWEPT_FACE",FACE,{"disambiguationData":[OSD([sQuery(id+"F10.wireOp",EDGE,"E7.sketch_text.stroke-17")])]});var subQ44=makeQuery(id+"F11.opExtrude","SWEPT_FACE",FACE,{"disambiguationData":[OSD([sQuery(id+"F10.wireOp",EDGE,"E7.sketch_text.stroke-0")])]});var subQ45=makeQuery(id+"F11.opExtrude","SWEPT_FACE",FACE,{"disambiguationData":[OSD([sQuery(id+"F10.wireOp",EDGE,"E7.sketch_text.stroke-10")])]});var subQ46=makeQuery(id+"F11.opExtrude","SWEPT_FACE",FACE,{"disambiguationData":[OSD([sQuery(id+"F10.wireOp",EDGE,"E7.sketch_text.stroke-15")])]});var subQ47=makeQuery(id+"F11.opExtrude","SWEPT_FACE",FACE,{"disambiguationData":[OSD([sQuery(id+"F10.wireOp",EDGE,"E7.sketch_text.stroke-18")])]});var subQ48=makeQuery(id+"F11.opExtrude","SWEPT_FACE",FACE,{"disambiguationData":[OSD([sQuery(id+"F10.wireOp",EDGE,"E7.sketch_text.stroke-21")])]});var subQ49=makeQuery(id+"F11.opExtrude","SWEPT_FACE",FACE,{"disambiguationData":[OSD([sQuery(id+"F10.wireOp",EDGE,"E7.sketch_text.stroke-22")])]});var subQ50=makeQuery(id+"F11.opExtrude","SWEPT_FACE",FACE,{"disambiguationData":[OSD([sQuery(id+"F10.wireOp",EDGE,"E7.sketch_text.stroke-24")])]});var subQ51=makeQuery(id+"F11.opExtrude","SWEPT_FACE",FACE,{"disambiguationData":[OSD([sQuery(id+"F10.wireOp",EDGE,"E7.sketch_text.stroke-26")])]});var subQ52=makeQuery(id+"F11.opExtrude","SWEPT_FACE",FACE,{"disambiguationData":[OSD([sQuery(id+"F10.wireOp",EDGE,"E7.sketch_text.stroke-28")])]});var subQ53=makeQuery(id+"F11.opExtrude","SWEPT_FACE",FACE,{"disambiguationData":[OSD([sQuery(id+"F10.wireOp",EDGE,"E7.sketch_text.stroke-29")])]});Q0=makeQuery(id+"F15.boolean.opBoolean","SPLIT",FACE,{"disambiguationData":[TD([subQ38])],"derivedFrom":makeQuery(id+"F11.boolean.opBoolean","SPLIT",FACE,{"disambiguationData":[TD([subQ38,subQ7,subQ32,subQ29,subQ20,subQ23,subQ42,subQ15,subQ11,subQ31,subQ26,subQ0,subQ44,subQ30,subQ18,subQ24,subQ17,subQ35,subQ16,subQ12,subQ1,subQ34,subQ45,subQ33,subQ21,subQ46,subQ40,subQ43,subQ47,subQ48,subQ49,subQ36,subQ50,subQ27,subQ51,subQ39,subQ52,subQ53])],"derivedFrom":makeQuery(id+"F5.boolean.opBoolean","SPLIT",FACE,{"disambiguationData":[TD([subQ38,subQ7,subQ32,subQ29,subQ20,subQ23,subQ42,subQ15,subQ11,subQ31,makeQuery(id+"F5.opExtrude","SWEPT_FACE",FACE,{"disambiguationData":[OSD([subQ2]),TDD([makeQuery(id+"F4.imprint","IMPRINT",EDGE,{"disambiguationData":[TD([[subQ4,-1.0]])],"derivedFrom":subQ2})])]}),subQ26])],"derivedFrom":makeQuery(id+"F3.boolean.opBoolean","COPY",FACE,{"derivedFrom":makeQuery(id+"F3.opExtrude","CAP_FACE",FACE,{"disambiguationData":[OSD([subQ37])],"isStart":false})})})})});}
            var sketch = newSketch(context, id + "F16", { "sketchPlane" : qUnion([Q0])});
            skText(sketch, "E10", { "text": "ALL", "fontName": "OpenSans-Italic.ttf"});
            const initialGuessF16  = {"E10": [-0.00825, -0.07112, 1, 0, 0.00762]};
            skSetInitialGuess(sketch, initialGuessF16);
            skSolve(sketch);
        }
        {
            var Q0;
            Q0 = qSketchRegion(id + "F16", true);
            extrude(context, id + "F17", {"entities" : qUnion([Q0]), "operationType" : NewBodyOperationType.ADD, "depth" : 7.62 * mm});
        }
    });
